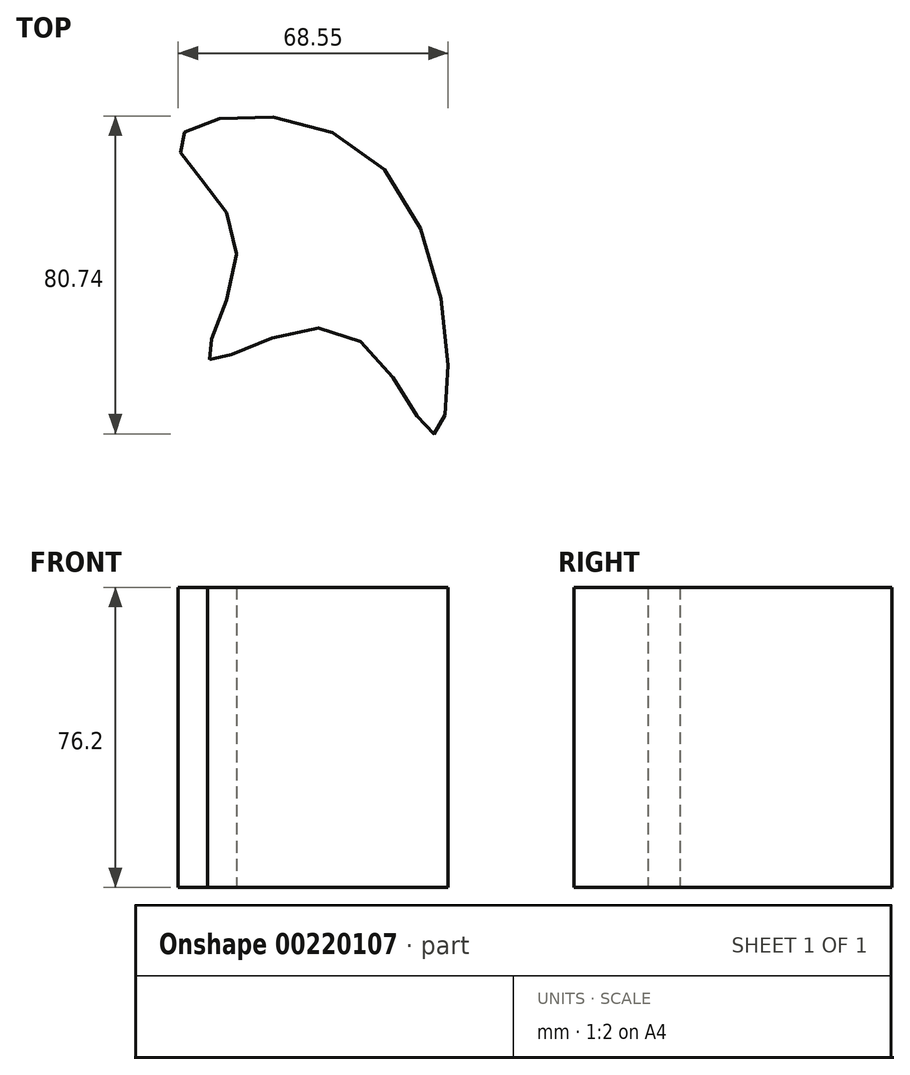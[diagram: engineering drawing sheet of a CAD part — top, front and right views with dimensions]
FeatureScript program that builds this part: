
annotation { "Feature Type Name" : "Feature", "Feature Type Description" : "" }
export const myFeature = defineFeature(function(context is Context, id is Id, definition is map)
    precondition{}
    {
        {
            var Q0;
            Q0=qCreatedBy(makeId("Top.planeOp"),FACE);
            var sketch = newSketch(context, id + "F0", { "sketchPlane" : qUnion([Q0])});
            skFitSpline(sketch, "E0", {"points": [v(-28.03, -30.98) * mm, v(5.59, -23.82) * mm, v(29.32, -49.9) * mm, v(15.32, 18.54) * mm, v(-35.73, 24.78) * mm, v(-21.39, 0) * mm, v(-28.03, -30.98) * mm]});
            skSolve(sketch);
        }
        {
            var Q0;
            Q0=makeQuery(id+"F0.imprint","IMPRINT",FACE,{"disambiguationData":[TD([[makeQuery(id+"F0.imprint","IMPRINT",EDGE,{"derivedFrom":sQuery(id+"F0.wireOp",EDGE,"E0")}),1.0]])]});
            extrude(context, id + "F1", {"entities" : qUnion([Q0]), "depth" : 76.2 * mm});
        }
    });
